# Revit family: QF_CAPIC_PILOTE_W296602
name_source: partatom
category: Equipement spécialisé
revit_build: Autodesk Revit 2018 (Build: 20170223_1515(x64)
units: mm (PartAtom-declared; Revit-internal decimal feet)

## family parameters
Basée sur le plan de construction = Non
Cote de connecteur circulaire = Utiliser le diamètre
Couper avec des vides une fois chargée = Non
Numéro OmniClass = 23.40.40.14
Partagée = Non
Point de calcul de pièce = Non
Titre OmniClass = Food Service Equipment
Toujours verticalement = Oui
Type d'élément = Normal

## types (1)
- 1700 x 925 x 450 mm
    Classification  Omniclass nombre et titre = 23.40.40.14
    Description = Sauteuse multifonction 60dm2
    Diamètre de Raccordement Eau Adoucie = 0 mm
    Diamètre de Raccordement Eau Chaude = 15 mm
    Diamètre de Raccordement Eau Froide = 15 mm
    Diamètre de Raccordement Evacuation = 0 mm
    Diamètre de Raccordement Gaz = 0 mm
    Débit Eau Adoucie = 0.0 L/s
    Débit Eau Chaude = 0.0 L/s
    Débit Eau Froide = 0.0 L/s
    Débit Gaz = 0.0 L/s
    Débit d'air d'extraction = 1350.0 m³/h
    Fabricant = CAPIC
    Fréquence = 50 Hz
    Hauteur de Raccordement Eau Adoucie du Sol Finis = 0 mm  [stored 0 ft]
    Hauteur de Raccordement Eau Chaude du Sol Finis = 600 mm
    Hauteur de Raccordement Eau Froide du Sol Finis = 600 mm
    Hauteur de Raccordement Evacuation Directe du Sol Finis = 0 mm  [stored 0 ft]
    Hauteur de Raccordement Gaz du Sol Finis = 0 mm  [stored 0 ft]
    Hauteur de Raccordement du Sol Finis = 550 mm
    Hauteur hors tout = 570 mm  [stored 1.87008 ft]
    Intensité nominale = 0 A
    Longueur hors tout = 1700 mm  [stored 5.57743 ft]
    Modèle = W296602
    Phase = 3
    Poids net à vide = 330.00 kg
    Pos Bec = 850 mm  [stored 2.78871 ft]
    Pression Maximum Eau Adoucie = 0.0 Pa
    Profondeur hors tout = 925 mm  [stored 3.03478 ft]
    Puissance Gaz kW = 0
    Puissance électrique  = 18000 W
    Tension = 400 V
    URL catalogue = http://www.capic-fr.com

note: [stored X ft] marks values corroborated as IEEE doubles in the binary element streams (Revit-internal decimal feet)
